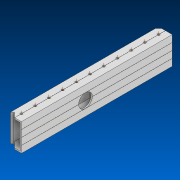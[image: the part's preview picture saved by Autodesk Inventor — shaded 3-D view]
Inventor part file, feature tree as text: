
AUTODESK INVENTOR PART (.ipt)
format: ipt  version: 2022.2 (Build 262287000, 287)  size: 535,552 bytes
history: native  units: in
note: dims shown in document units (in); Inventor stores cm internally (conversion verified against a paired STEP export)
features: other x16, extrude x4, sketch x4, pattern_linear x1, reference x1
ambient origin geometry x8: Origin, YZ Plane, XZ Plane, XY Plane, X Axis, Y Axis, Z Axis, Center Point
bodies: Solid1 (feature_tree)
feature tree (26):
  extrude  "Extrusion1"  Depth=2.0in
  other  "Work Axis1"
  pattern_linear  "Rectangular Pattern1"  Count1=11  [1 undecoded]
  extrude  "Extrusion2"  TaperAngle=0.0deg  [1 undecoded]
  extrude  "Extrusion3"  Depth=1.0in
  extrude  "Extrusion4"  TaperAngle=0.0deg  [1 undecoded]
  sketch  "Sketch1"  dims[d0=1.0in d1=2.0in]
  other  "Work Axis2"
  other  "Work Axis3"
  other  "Work Axis4"
  other  "Work Axis5"
  other  "Work Axis6"
  other  "Work Axis7"
  other  "Work Axis8"
  other  "Work Axis9"
  other  "Work Axis10"
  sketch  "Sketch2"  dims[d2=48.0in]
  sketch  "Sketch3"  dims[d3=0.0in d4=4.3307in]
  other  "Work Axis60"
  reference  "Reference3"
  sketch  "Sketch4"  dims[d6=1.0in d9=0.0in d10=0.0in d11=1.0in d12=0.0in d13=0.0in d15=0.3in d16=45.0deg d17=0.5in d18=0.1in d19=0.0in]
  other  "Cut-Extrude2"
  parser-record x1  (decoder bookkeeping rows leaked as tree rows — omitted from the tree; the rows remain in map.json)
  other  "Chassis.iam"
  other  "Plastic Clamping Bearing Block (217-4155):5"
  other  "217-4155-001 Rev6_2"
note: 3 required parameter values undecoded (feature->parameter linkage not recoverable at this tier; creation-order binding heuristic only, values carry confidence <= 0.55)
note: 1 file-system path scrubbed to <path> (originals preserved in map.json)
